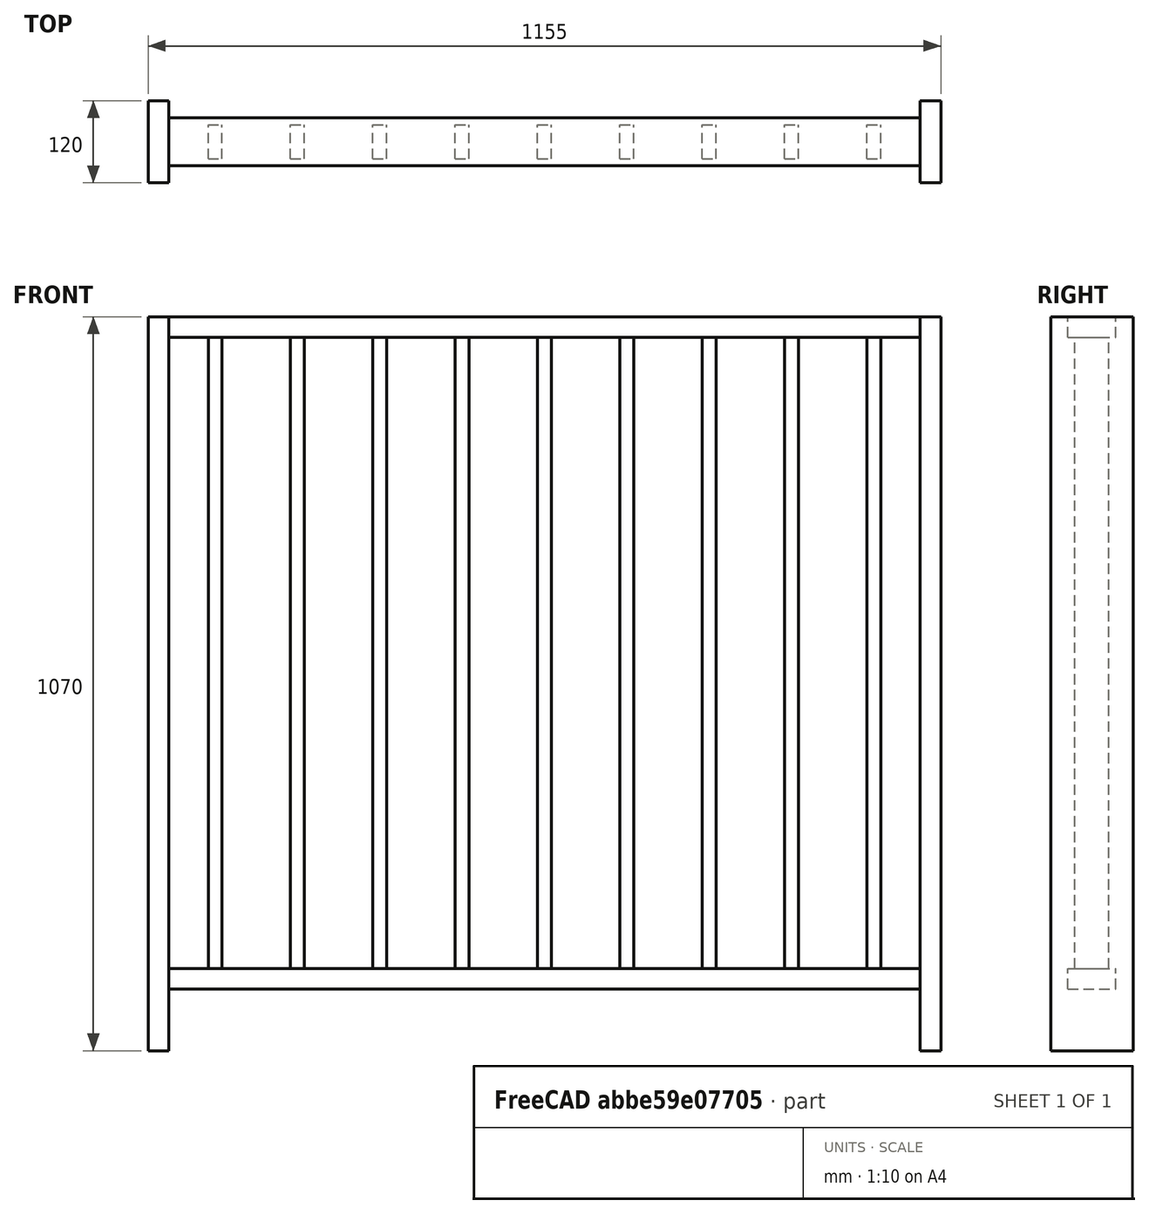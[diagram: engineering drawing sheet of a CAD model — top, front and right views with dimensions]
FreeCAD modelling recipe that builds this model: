
FCSTD DOCUMENT  (FreeCAD 0.18R16146 (Git))
Label: guarda-corpo-grade-modulo-2
License: All rights reserved
LicenseURL: http://en.wikipedia.org/wiki/All_rights_reserved
objects: Part::Box×5, Spreadsheet::Sheet×1, Part::FeaturePython×1, Part::Compound×1, Part::Feature×1
note: 8 computed .brp shape members not serialized (recipe doc carries the construction recipe); baked Part::Feature solids carry a one-line shape summary decoded from their .brp

FEATURE [Spreadsheet::Sheet] Spreadsheet  label="medidas"
  cells = B1=altura (height); C1=frente (length); D1=profundidade (width); E1=z; F1=x; G1=y; H1=quantidade; A2=pe_direito_1; B2(pe_direito_1_height)=1070; C2(pe_direito_1_length)=30; D2(pe_direito_1_width)=120; E2(pe_direito_1_z)=0; F2(pe_direito_1_x)=0; G2(pe_direito_1_y)=0; H2=1; A3=pe_direito_2; B3(pe_direito_2_height)=1070; C3(pe_direito_2_length)=30; D3(pe_direito_2_width)=120; E3(pe_direito_2_z)=0; F3(pe_direito_2_x)=1125; G3(pe_direito_2_y)=0; H3=1; A4=travessa_inferior; B4(travessa_inferior_height)=30; C4(travessa_inferior_length)=1095; D4(travessa_inferior_width)=70; E4(travessa_inferior_z)=90; F4(travessa_inferior_x)=30; G4(travessa_inferior_y)=25; H4=1; A5=travessa_superior; B5(travessa_superior_height)=30; C5(travessa_superior_length)=1095; D5(travessa_superior_width)=70; E5(travessa_superior_z)=1040; F5(travessa_superior_x)=30; G5(travessa_superior_y)=25; H5=1; A6=palito_grade; B6(palito_grade_height)=920; C6(palito_grade_length)=20; D6(palito_grade_width)=50; E6(palito_grade_z)=0; F6(palito_grade_x)=0; G6(palito_grade_y)=0; H6=1; A7=palitos; C7(palitos_length)=120; E7(palitos_z)=120; F7(palitos_x)=87.5; G7(palitos_y)=35; H7(palitos_qty)=9
FEATURE [Part::Box] Box  label="pe_direito_1"
  AttacherType = Attacher::AttachEngine3D
  Height = 1070
  Length = 30
  Width = 120
  expr: Placement.Base.z = medidas.pe_direito_1_z
  expr: Placement.Base.y = medidas.pe_direito_1_y
  expr: Placement.Base.x = medidas.pe_direito_1_x
  expr: Height = medidas.pe_direito_1_height
  expr: Width = medidas.pe_direito_1_width
  expr: Length = medidas.pe_direito_1_length
FEATURE [Part::Box] Box001  label="pe_direito_2"
  AttacherType = Attacher::AttachEngine3D
  Height = 1070
  Length = 30
  Placement = pos=(1125,0,0) rot=(0,0,1;0rad)
  Width = 120
  expr: Placement.Base.z = medidas.pe_direito_2_z
  expr: Placement.Base.y = medidas.pe_direito_2_y
  expr: Placement.Base.x = medidas.pe_direito_2_x
  expr: Height = medidas.pe_direito_2_height
  expr: Width = medidas.pe_direito_2_width
  expr: Length = medidas.pe_direito_2_length
FEATURE [Part::Box] Box002  label="travessa_inferior"
  AttacherType = Attacher::AttachEngine3D
  Height = 30
  Length = 1095
  Placement = pos=(30,25,90) rot=(0,0,1;0rad)
  Width = 70
  expr: Placement.Base.z = medidas.travessa_inferior_z
  expr: Placement.Base.y = medidas.travessa_inferior_y
  expr: Placement.Base.x = medidas.travessa_inferior_x
  expr: Height = medidas.travessa_inferior_height
  expr: Width = medidas.travessa_inferior_width
  expr: Length = medidas.travessa_inferior_length
FEATURE [Part::Box] Box003  label="travessa_superior"
  AttacherType = Attacher::AttachEngine3D
  Height = 30
  Length = 1095
  Placement = pos=(30,25,1040) rot=(0,0,1;0rad)
  Width = 70
  expr: Placement.Base.z = medidas.travessa_superior_z
  expr: Placement.Base.y = medidas.travessa_superior_y
  expr: Placement.Base.x = medidas.travessa_superior_x
  expr: Height = medidas.travessa_superior_height
  expr: Width = medidas.travessa_superior_width
  expr: Length = medidas.travessa_superior_length
FEATURE [Part::Box] Box004  label="palito_grade"
  AttacherType = Attacher::AttachEngine3D
  Height = 920
  Length = 20
  Width = 50
  expr: Placement.Base.z = medidas.palito_grade_z
  expr: Placement.Base.y = medidas.palito_grade_y
  expr: Placement.Base.x = medidas.palito_grade_x
  expr: Height = medidas.palito_grade_height
  expr: Width = medidas.palito_grade_width
  expr: Length = medidas.palito_grade_length
FEATURE [Part::FeaturePython] Array  label="palitos"  # Draft array (typed FeaturePython)
  Angle = 360
  ArrayType = 0
  Axis = (0,0,1)
  Base = -> Box004
  Center = (0,0,0)
  Fuse = false
  IntervalAxis = (0,0,0)
  IntervalX = (120,0,0)
  IntervalY = (0,1,0)
  IntervalZ = (0,0,1)
  NumberPolar = 1
  NumberX = 9
  NumberY = 1
  NumberZ = 1
  Placement = pos=(87.5,35,120) rot=(0,0,1;0rad)
  expr: IntervalX.x = medidas.palitos_length
  expr: NumberX = medidas.palitos_qty
  expr: Placement.Base.z = medidas.palitos_z
  expr: Placement.Base.y = medidas.palitos_y
  expr: Placement.Base.x = medidas.palitos_x
FEATURE [Part::Compound] Compound  label="modulo_2"
  Links = -> [Box,Box001,Box002,Box003,Array]
FEATURE [Part::Feature] Compound001  label="modulo_2_copy"
  shape: bbox 1155 x 120 x 1070 mm, 78 faces, 13 solids (baked)
